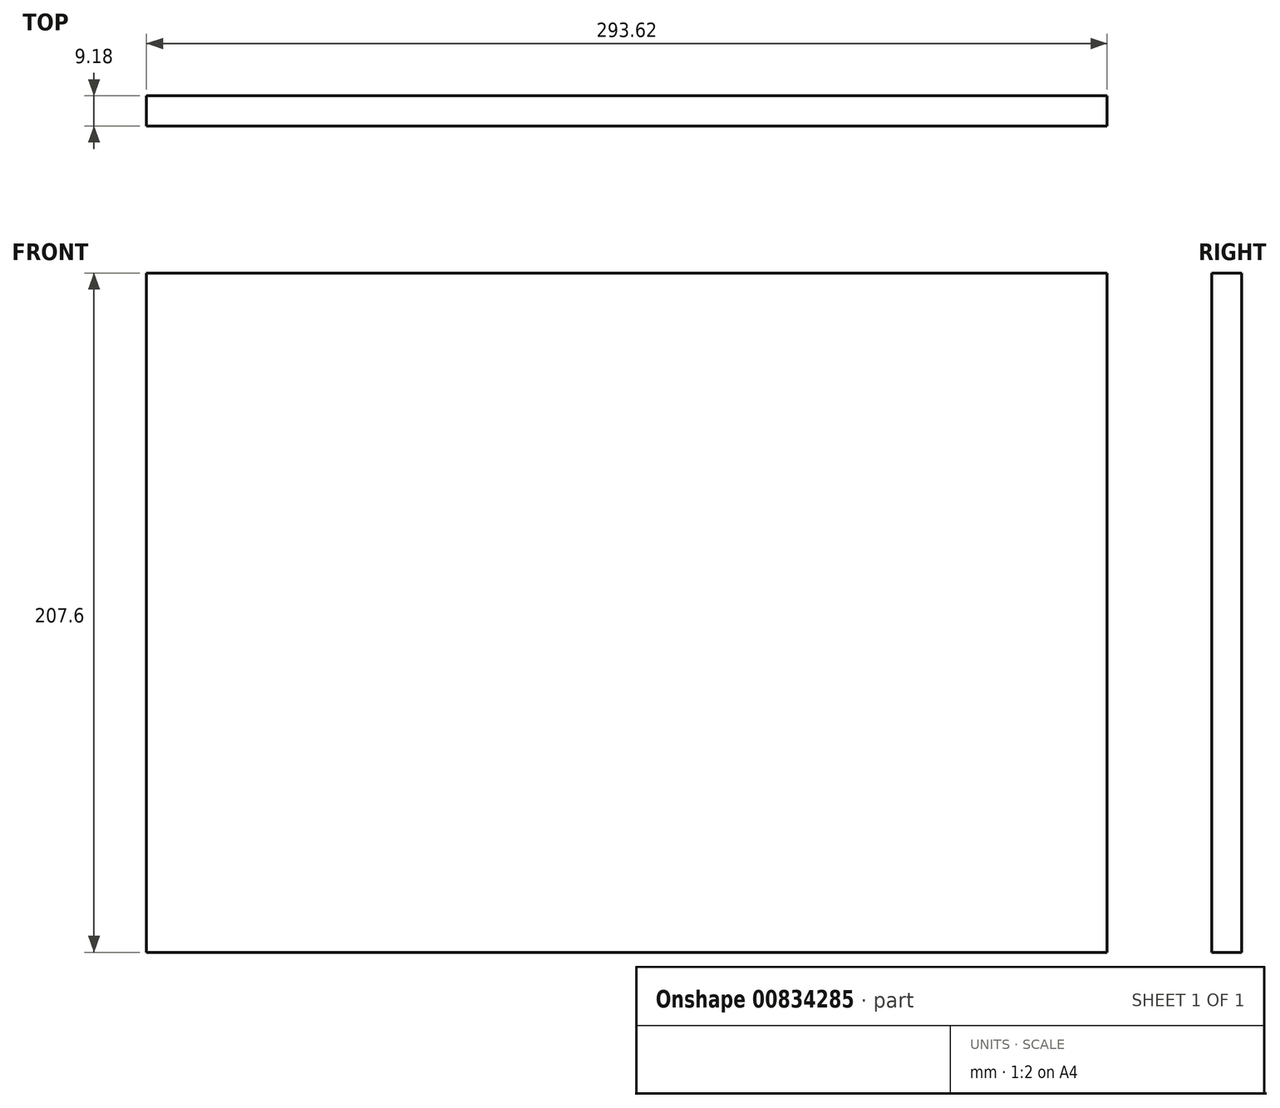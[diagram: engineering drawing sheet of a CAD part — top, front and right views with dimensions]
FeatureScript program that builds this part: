
annotation { "Feature Type Name" : "Feature", "Feature Type Description" : "" }
export const myFeature = defineFeature(function(context is Context, id is Id, definition is map)
    precondition{}
    {
        {
            var Q0;
            Q0=qCreatedBy(makeId("Top.planeOp"),FACE);
            var sketch = newSketch(context, id + "F0", { "sketchPlane" : qUnion([Q0])});
            skLineSegment(sketch, "E0.bottom", {"start": v(-146.81, 4.59) * mm, "end": v(146.81, 4.59) * mm});
            skLineSegment(sketch, "E0.top", {"start": v(-146.81, -4.59) * mm, "end": v(146.81, -4.59) * mm});
            skLineSegment(sketch, "E0.left", {"start": v(-146.81, 4.59) * mm, "end": v(-146.81, -4.59) * mm});
            skLineSegment(sketch, "E0.right", {"start": v(146.81, 4.59) * mm, "end": v(146.81, -4.59) * mm});
            skPoint(sketch, "E0.middle", {"position": v(0, 0) * mm});
            skSolve(sketch);
        }
        {
            var Q0;
            Q0=makeQuery(id+"F0.imprint","IMPRINT",FACE,{"disambiguationData":[TD([[makeQuery(id+"F0.imprint","IMPRINT",EDGE,{"derivedFrom":sQuery(id+"F0.wireOp",EDGE,"E0.bottom")}),-1.0]])]});
            var Q1;
            Q1=sQuery(id+"F0.wireOp",EDGE,"E0.bottom");
            extrude(context, id + "F1", {"entities" : qUnion([Q0]), "surfaceEntities" : qUnion([Q1]), "endBound" : BoundingType.SYMMETRIC, "depth" : 207.6 * mm, "offsetDistance" : 25.4 * mm});
        }
    });
